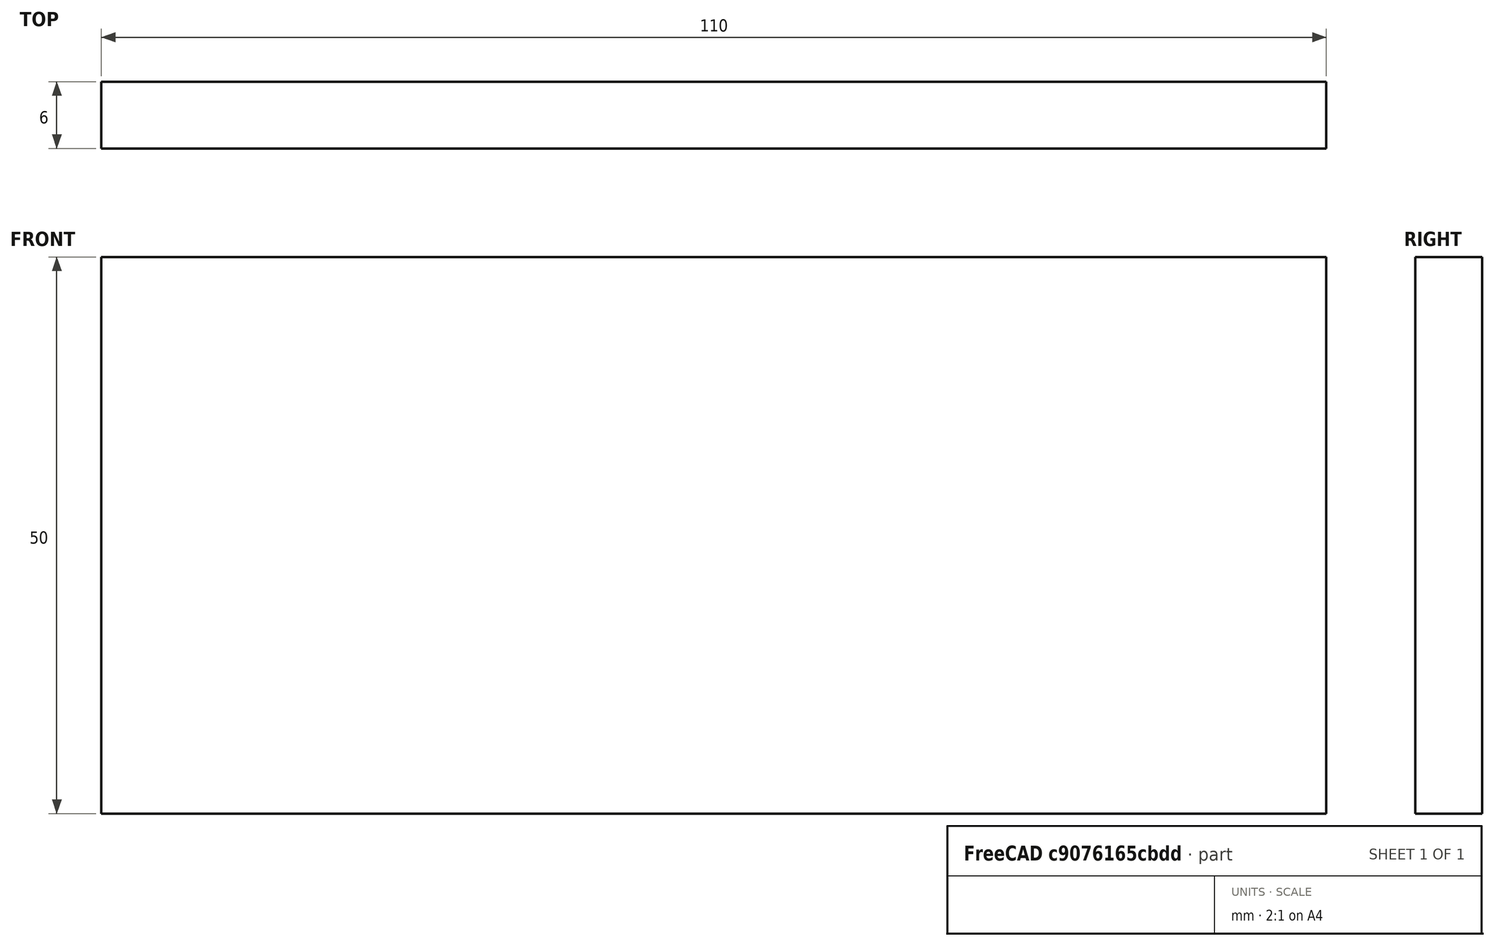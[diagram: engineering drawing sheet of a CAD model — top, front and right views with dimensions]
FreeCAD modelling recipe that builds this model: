
FCSTD DOCUMENT  (FreeCAD 0.15R4671 (Git))
Label: Flat Bar 110x6 EN10058 S235JR
License: All rights reserved
LicenseURL: http://en.wikipedia.org/wiki/All_rights_reserved
objects: Sketcher::SketchObject×1, Part::Extrusion×1
note: 2 computed .brp shape members not serialized (recipe doc carries the construction recipe); baked Part::Feature solids carry a one-line shape summary decoded from their .brp

FEATURE [Sketcher::SketchObject] Sketch
  sketch-geometry (4):
    g0: LineSegment StartX=-55 StartY=-3 StartZ=0 EndX=55 EndY=-3 EndZ=0
    g1: LineSegment StartX=55 StartY=-3 StartZ=0 EndX=55 EndY=3 EndZ=0
    g2: LineSegment StartX=55 StartY=3 StartZ=0 EndX=-55 EndY=3 EndZ=0
    g3: LineSegment StartX=-55 StartY=3 StartZ=0 EndX=-55 EndY=-3 EndZ=0
  constraints (12):
    c: Coincident(g0,g1)
    c: Coincident(g1,g2)
    c: Coincident(g2,g3)
    c: Coincident(g3,g0)
    c: Horizontal(g0)
    c: Horizontal(g2)
    c: Vertical(g1)
    c: Vertical(g3)
    c: Symmetric(g1,g2,g-2)
    c: Symmetric(g0,g1,g-1)
    c: DistanceY(g1) = 6
    c: DistanceX(g0) = 110
FEATURE [Part::Extrusion] Extrude  label="Flat Bar 110x6 EN10058 S235JR"
  Base = -> Sketch
  Dir = (0,0,50)
  Solid = true
